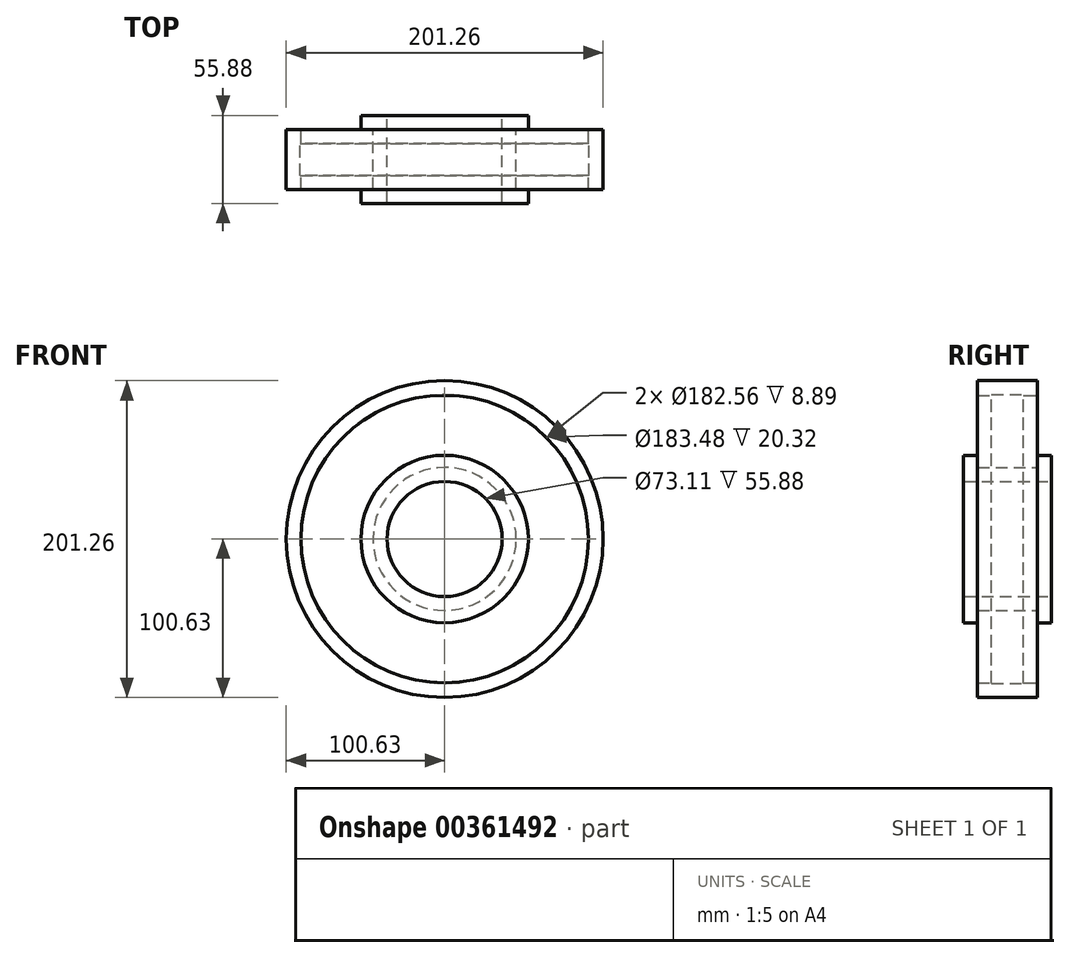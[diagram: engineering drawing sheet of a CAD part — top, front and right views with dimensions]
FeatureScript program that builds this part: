
annotation { "Feature Type Name" : "Feature", "Feature Type Description" : "" }
export const myFeature = defineFeature(function(context is Context, id is Id, definition is map)
    precondition{}
    {
        {
            var Q0;
            Q0=qCreatedBy(makeId("Front.planeOp"),FACE);
            var sketch = newSketch(context, id + "F0", { "sketchPlane" : qUnion([Q0])});
            skCircle(sketch, "E0", {"center": v(0, 0) * mm, "radius": 91.28 * mm});
            skCircle(sketch, "E1", {"center": v(0, 0) * mm, "radius": 53.18 * mm});
            skCircle(sketch, "E2", {"center": v(0, 0) * mm, "radius": 45.44 * mm});
            skCircle(sketch, "E3", {"center": v(0, 0) * mm, "radius": 100.63 * mm});
            skSolve(sketch);
        }
        {
            var Q0;
            Q0 = qSketchRegion(id + "F0", true);
            var Q1;
            Q1=makeQuery(id+"F0.imprint","IMPRINT",FACE,{"disambiguationData":[TD([[makeQuery(id+"F0.imprint","IMPRINT",EDGE,{"derivedFrom":sQuery(id+"F0.wireOp",EDGE,"E1")}),1.0]])]});
            extrude(context, id + "F1", {"entities" : qUnion([Q0, Q1]), "depth" : 38.1 * mm});
        }
        {
            var Q0;
            Q0=makeQuery(id+"F1.opExtrude","SWEPT_FACE",FACE,{"disambiguationData":[OSD([sQuery(id+"F0.wireOp",EDGE,"E0")])]});
            shell(context, id + "F2", {"entities" : qUnion([Q0]), "thickness" : 8.9 * mm});
        }
        {
            var Q0;
            Q0=makeQuery(id+"F1.opExtrude","SWEPT_FACE",FACE,{"disambiguationData":[OSD([sQuery(id+"F0.wireOp",EDGE,"E1")])]});
            shell(context, id + "F3", {"entities" : qUnion([Q0]), "thickness" : 8.9 * mm, "oppositeDirection" : true});
        }
    });
